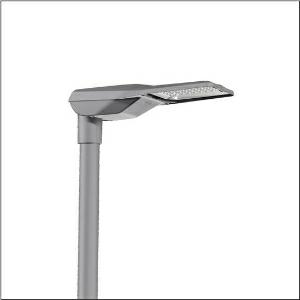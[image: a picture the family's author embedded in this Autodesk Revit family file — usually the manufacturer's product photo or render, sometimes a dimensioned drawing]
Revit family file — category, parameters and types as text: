
# Revit family: streetlight_sl_21_iq_mini___st0_5a_5xe2b41d08gb_120c
name_source: partatom
category: Lighting Fixtures
units: mm (PartAtom-declared; Revit-internal decimal feet)

## family parameters
Cut with Voids When Loaded = No
Host = Face
Light Source = No
Part Type = Normal
Room Calculation Point = No
Round Connector Dimension = Use Diameter
Shared = No

## types (1)
- --- (1 x LED, 5920 lm, 37.1 W, 4000K)
    Apparent Load = 37 VA
    CIE Flux Codes = 41 75 97 100 100
    Color Rendering = 70
    Color Temperature = 4000K
    Default Elevation = 1800 mm
    Description = Streetlight SL 21 mini, mast luminaire, primary light control with lens, of PMMA, primary optical cover: cover, of toughened safety glass, transparent, light distribution: ST0.5a, light emission: direct distribution, primary light characteristic: asymmetric, installation type: post-top, side-entry, LED, High Power LED, rated luminous flux: 5.920lm, luminous efficacy: 160lm/W, light colour: 740, colour temperature: 4000K, control gear: ECG iQ, control: Auto-Match, Temp-Guard, Lumen-Switch, Night-Set, Smart-Wire, Light-Fading, Desk-Remote (wireless, voltage-free reading and setting of iQ features in the workshop via application-optimized NFC function/RFID function), optimised constant luminous flux control (CLO 2.0), mains connection: 220..240V, AC, 50/60Hz, start of lifetime: 37W, end of lifetime: 39W, reduction: 18W, luminaire housing, of diecast aluminium, powder-coated, Siteco® metallic grey (DB 702S), corrosivity category C5 according to DIN EN ISO 12944, length: 628mm, width: 235mm, height: 110mm, spigot size: 60/76mm (post-top) and 42/60/76mm (side-entry), mast flange for spigot size: 42mm: 5XC10008XM4, 60mm: 5XC10008XM2, 76/60mm: 5XC10108XM1, protection rating (complete): IP66, insulation class (complete): insulation class II (safety insulation), certification: CE, ENEC, VDE, impact resistance: IK09, permissible operating ambient temperature for outdoor applications: -40..+50°C, standard-compliant lighting for roads and squares, packaging unit: 1 piece

Light Distribution: ST0.5a
    Height = 110 mm
    Lamp = 1 x LED
    Lamp Light Flux = 5920 lm
    Lamp Power = 37.1 W
    Lamp count = 1
    Length = 625 mm
    Luminous efficacy = 160 lm/W
    Manufacturer = Siteco
    ModVariant = No
    Model = 5XE2B41D08GB
    Number of Poles = 1
    OnlyDefault = Yes
    Power Factor = 1
    Product Name = Streetlight SL 21 iQ mini | ST0.5a
    Product group = mast luminaire | pylon top
    ProductGroupID = 6100
    Protection Class = Protection class II
    Protection Degree = IP 66
    RLX_Detail_Level = 1
    RlxData = <blob elided: 103069 chars, md5=5fb0d497>
    Socket = socket
    Standby Power = 0 W
    System Light Flux = 5920 lm
    System Power = 37 W
    Type Comments = factory setting: luminous flux: 100 % | dim-lin: 254 | 385 mA
    Type Image = l_1003519.jpg
    URL = http://relux.com
    VarID = @adj_111301
    Voltage = 0 V
    Weight = 0.00 kg
    Width = 234 mm

## geometry (parser evidence)
native form markers: Blend x4, Sweep x10
no freeform markers — native parametric forms only
